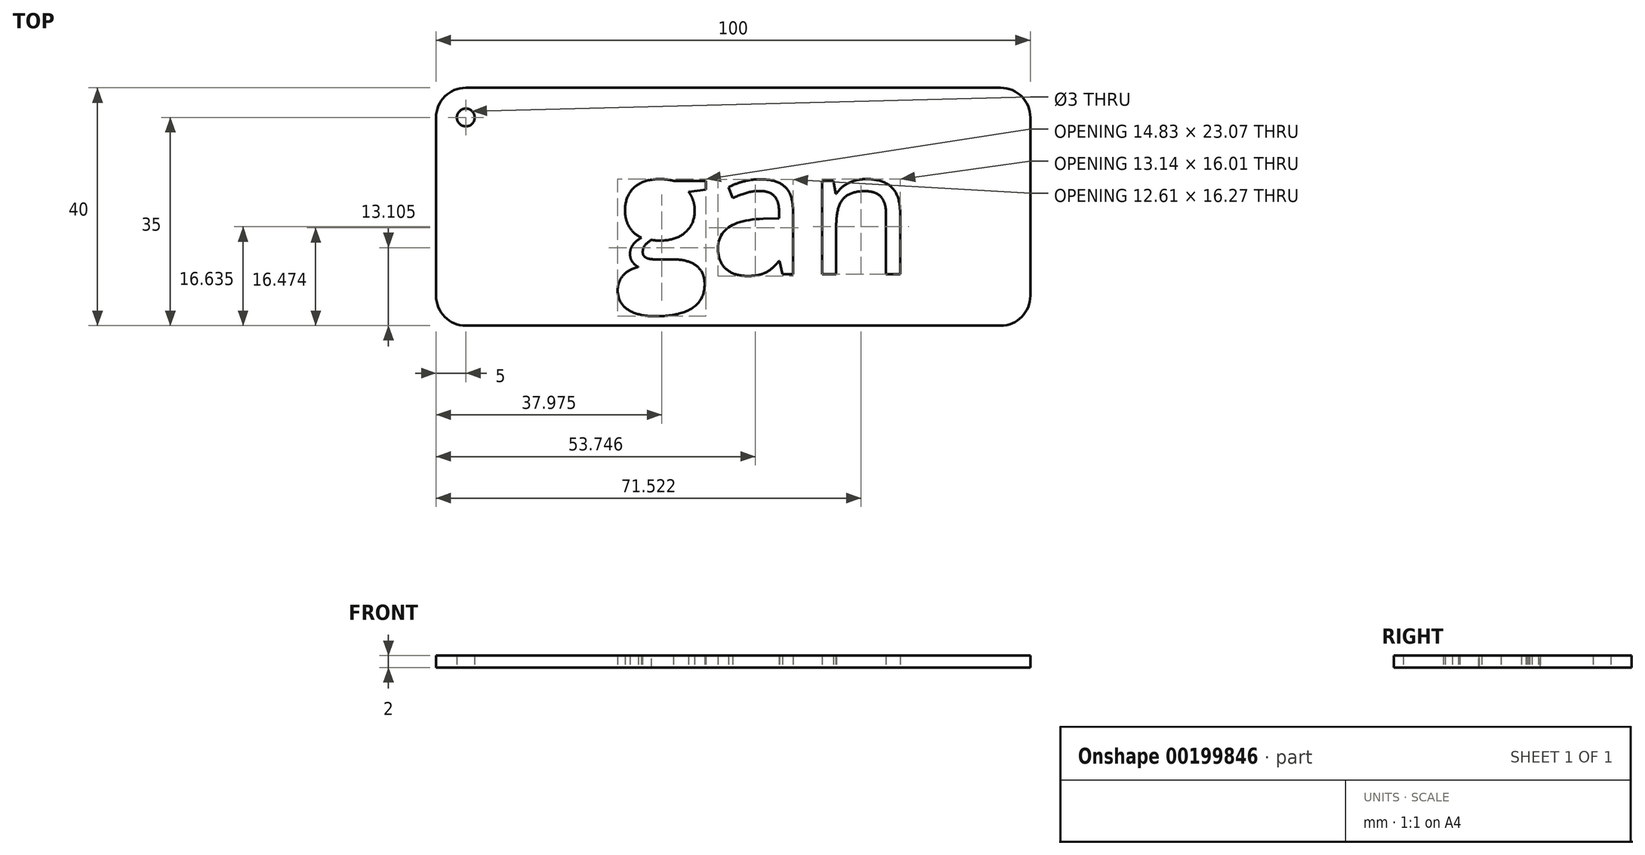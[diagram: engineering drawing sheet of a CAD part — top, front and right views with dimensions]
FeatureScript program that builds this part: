
annotation { "Feature Type Name" : "Feature", "Feature Type Description" : "" }
export const myFeature = defineFeature(function(context is Context, id is Id, definition is map)
    precondition{}
    {
        {
            var Q0;
            Q0=qCreatedBy(makeId("Top.planeOp"),FACE);
            var sketch = newSketch(context, id + "F0", { "sketchPlane" : qUnion([Q0])});
            skLineSegment(sketch, "E0.bottom", {"start": v(5, 40) * mm, "end": v(95, 40) * mm});
            skLineSegment(sketch, "E0.top", {"start": v(5, 0) * mm, "end": v(95, 0) * mm});
            skLineSegment(sketch, "E0.left", {"start": v(0, 35) * mm, "end": v(0, 5) * mm});
            skLineSegment(sketch, "E0.right", {"start": v(100, 35) * mm, "end": v(100, 5) * mm});
            skPoint(sketch, "E1.visualSharp", {"position": v(0, 40) * mm});
            skArc(sketch, "E1.filletArc", {"start": v(5, 40) * mm, "mid": v(1.46, 38.54) * mm, "end": v(0, 35) * mm});
            skPoint(sketch, "E2.visualSharp", {"position": v(0, 0) * mm});
            skArc(sketch, "E2.filletArc", {"start": v(0, 5) * mm, "mid": v(1.46, 1.46) * mm, "end": v(5, 0) * mm});
            skPoint(sketch, "E3.visualSharp", {"position": v(100, 0) * mm});
            skArc(sketch, "E3.filletArc", {"start": v(95, 0) * mm, "mid": v(98.54, 1.46) * mm, "end": v(100, 5) * mm});
            skPoint(sketch, "E4.visualSharp", {"position": v(100, 40) * mm});
            skArc(sketch, "E4.filletArc", {"start": v(100, 35) * mm, "mid": v(98.54, 38.54) * mm, "end": v(95, 40) * mm});
            skCircle(sketch, "E5", {"center": v(5, 35) * mm, "radius": 1.5 * mm});
            skText(sketch, "E6", { "text": "gan", "fontName": "OpenSans-Regular.ttf"});
            const initialGuessF0  = {"E6": [0.03, 0.00863, 1, 0, 0.02115]};
            skSetInitialGuess(sketch, initialGuessF0);
            skSolve(sketch);
        }
        {
            var Q0;
            Q0 = qSketchRegion(id + "F0", true);
            extrude(context, id + "F1", {"entities" : qUnion([Q0]), "depth" : 2 * mm});
        }
    });
